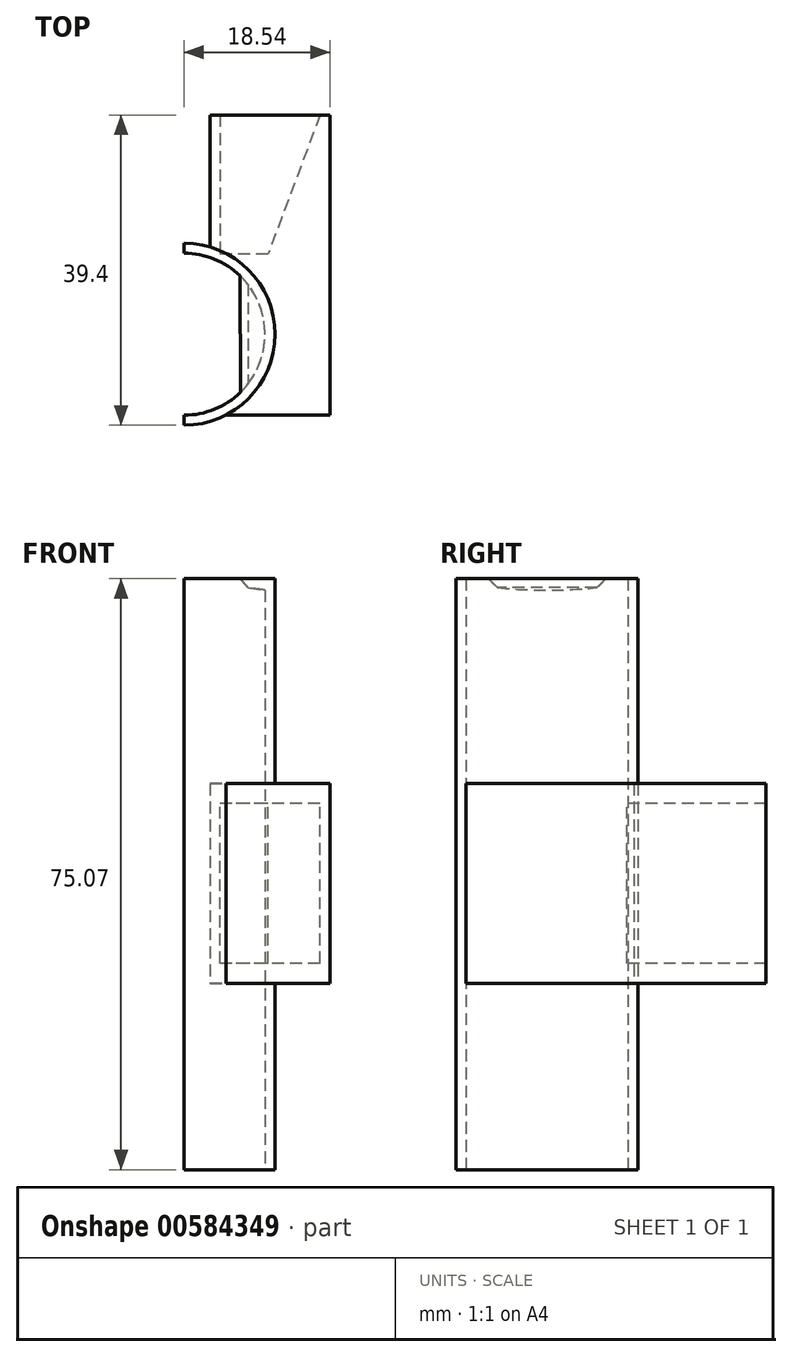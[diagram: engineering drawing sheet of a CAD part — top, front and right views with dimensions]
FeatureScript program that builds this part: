
annotation { "Feature Type Name" : "Feature", "Feature Type Description" : "" }
export const myFeature = defineFeature(function(context is Context, id is Id, definition is map)
    precondition{}
    {
        {
            var Q0;
            Q0=qCreatedBy(makeId("Top.planeOp"),FACE);
            var sketch = newSketch(context, id + "F0", { "sketchPlane" : qUnion([Q0])});
            skArc(sketch, "E0", {"start": v(0, -10.29) * mm, "mid": v(10.29, 0) * mm, "end": v(0, 10.29) * mm});
            skArc(sketch, "E1", {"start": v(0, -11.56) * mm, "mid": v(11.56, 0) * mm, "end": v(0, 11.56) * mm});
            skLineSegment(sketch, "E2", {"start": v(0, 11.56) * mm, "end": v(0, 10.29) * mm});
            skLineSegment(sketch, "E3.trimOffspring", {"start": v(0, -10.29) * mm, "end": v(0, -11.56) * mm});
            skSolve(sketch);
        }
        {
            var Q0;
            Q0=qSketchRegion(id+"F0",true);
            extrude(context, id + "F1", {"entities" : qUnion([Q0]), "endBound" : BoundingType.SYMMETRIC, "depth" : 75.9 * mm});
        }
        {
            var Q0;
            Q0=makeQuery(id+"F1.opExtrude","CAP_FACE",FACE,{"disambiguationData":[OSD([sQuery(id+"F0.wireOp",EDGE,"E0"),sQuery(id+"F0.wireOp",EDGE,"E1"),sQuery(id+"F0.wireOp",EDGE,"E2"),sQuery(id+"F0.wireOp",EDGE,"E3.trimOffspring")])],"isStart":false});
            var sketch = newSketch(context, id + "F2", { "sketchPlane" : qUnion([Q0])});
            skArc(sketch, "E4", {"start": v(0, -11.56) * mm, "mid": v(11.56, 0) * mm, "end": v(0, 11.56) * mm});
            skLineSegment(sketch, "E5", {"start": v(0, 11.56) * mm, "end": v(0, -11.56) * mm});
            skSolve(sketch);
        }
        {
            var Q0;
            Q0=qSketchRegion(id+"F2",true);
            extrude(context, id + "F3", {"entities" : qUnion([Q0]), "operationType" : NewBodyOperationType.ADD, "endBound" : BoundingType.SYMMETRIC, "depth" : 1.52 * mm});
        }
        {
            var Q0;
            Q0=makeQuery(id+"F3.opExtrude","CAP_EDGE",EDGE,{"disambiguationData":[OSD([sQuery(id+"F2.wireOp",EDGE,"E5")])],"isStart":true});
            chamfer(context, id + "F4", {"entities" : qUnion([Q0]), "chamferType" : ChamferType.OFFSET_ANGLE, "width" : 1.52 * mm, "oppositeDirection" : false, "angle" : 82 * degree, "tangentPropagation" : true});
        }
        {
            var Q0;
            Q0=makeQuery(id+"F4.opChamfer","SPLIT",FACE,{"disambiguationData":[OD(0.0)],"derivedFrom":makeQuery(id+"F3.boolean.opBoolean","MERGE",FACE,{"derivedFrom":[makeQuery(id+"F1.opExtrude","SWEPT_FACE",FACE,{"disambiguationData":[OSD([sQuery(id+"F0.wireOp",EDGE,"E2")])]}),makeQuery(id+"F1.opExtrude","SWEPT_FACE",FACE,{"disambiguationData":[OSD([sQuery(id+"F0.wireOp",EDGE,"E3.trimOffspring")])]}),makeQuery(id+"F3.opExtrude","SWEPT_FACE",FACE,{"disambiguationData":[OSD([sQuery(id+"F2.wireOp",EDGE,"E5")])]})]})});
            var sketch = newSketch(context, id + "F5", { "sketchPlane" : qUnion([Q0])});
            skLineSegment(sketch, "E6.bottom", {"start": v(-11.56, -37.95) * mm, "end": v(11.56, -37.95) * mm});
            skLineSegment(sketch, "E6.top", {"start": v(-11.56, -36.36) * mm, "end": v(11.56, -36.36) * mm});
            skLineSegment(sketch, "E6.left", {"start": v(-11.56, -37.95) * mm, "end": v(-11.56, -36.36) * mm});
            skLineSegment(sketch, "E6.right", {"start": v(11.56, -37.95) * mm, "end": v(11.56, -36.36) * mm});
            skSolve(sketch);
        }
        {
            var Q0;
            Q0=qSketchRegion(id+"F5",true);
            extrude(context, id + "F6", {"entities" : qUnion([Q0]), "operationType" : NewBodyOperationType.REMOVE, "oppositeDirection" : true, "depth" : 25.4 * mm});
        }
        {
            var Q0;
            Q0=makeQuery(id+"F6.boolean.opBoolean","COPY",FACE,{"derivedFrom":makeQuery(id+"F6.opExtrude","SWEPT_FACE",FACE,{"disambiguationData":[OSD([sQuery(id+"F5.wireOp",EDGE,"E6.top")])]})});
            cPlane(context, id + "F7", {"entities" : qUnion([Q0]), "cplaneType" : CPlaneType.OFFSET, "offset" : ((3.5 - 0.51) / 2) * mm, "oppositeDirection" : true, "width" : 152.4 * mm, "height" : 152.4 * mm});
        }
        {
            var Q0;
            Q0=makeQuery(id+"F3.opExtrude","CAP_FACE",FACE,{"disambiguationData":[OSD([sQuery(id+"F2.wireOp",EDGE,"E4"),sQuery(id+"F2.wireOp",EDGE,"E5")])],"isStart":false});
            var sketch = newSketch(context, id + "F8", { "sketchPlane" : qUnion([Q0])});
            skLineSegment(sketch, "E7", {"start": v(7, 7.54) * mm, "end": v(7.07, -7.47) * mm});
            skLineSegment(sketch, "E8", {"start": v(0, 11.56) * mm, "end": v(0, -11.56) * mm});
            skPoint(sketch, "E9.center.orphan", {"position": v(0, 0) * mm});
            skArc(sketch, "E10", {"start": v(0, -10.29) * mm, "mid": v(3.8, -9.56) * mm, "end": v(7.07, -7.47) * mm});
            skArc(sketch, "E11.trimOffspring", {"start": v(7, 7.54) * mm, "mid": v(3.76, 9.58) * mm, "end": v(0, 10.29) * mm});
            skSolve(sketch);
        }
        {
            var Q0;
            {var subQ0=sQuery(id+"F8.wireOp",EDGE,"E7");Q0=makeQuery(id+"F8.imprint","IMPRINT",FACE,{"disambiguationData":[TD([[makeQuery(id+"F8.imprint","IMPRINT",EDGE,{"derivedFrom":subQ0}),-1.0]])]});}
            extrude(context, id + "F9", {"entities" : qUnion([Q0]), "operationType" : NewBodyOperationType.REMOVE, "oppositeDirection" : true, "depth" : 25.4 * mm, "offsetDistance" : 25.4 * mm});
        }
        {
            var Q0;
            Q0=makeQuery(id+"F9.boolean.opBoolean","INTERSECT",EDGE,{"derivedFrom":[makeQuery(id+"F4.opChamfer","BLEND_FACE",FACE,{"disambiguationData":[OSD([sQuery(id+"F2.wireOp",EDGE,"E5")])]}),makeQuery(id+"F9.opExtrude","SWEPT_FACE",FACE,{"disambiguationData":[OSD([sQuery(id+"F8.wireOp",EDGE,"E7")])]})]});
            chamfer(context, id + "F10", {"entities" : qUnion([Q0]), "width" : 1.27 * mm, "tangentPropagation" : true});
        }
        {
            var Q0;
            Q0=qCreatedBy(makeId("Front.planeOp"),FACE);
            cPlane(context, id + "F11", {"entities" : qUnion([Q0]), "cplaneType" : CPlaneType.OFFSET, "offset" : 10.16 * mm, "oppositeDirection" : true, "width" : 152.4 * mm, "height" : 152.4 * mm});
        }
        {
            var Q0;
            Q0=qCreatedBy(id+"F11.planeOp",FACE);
            var sketch = newSketch(context, id + "F12", { "sketchPlane" : qUnion([Q0])});
            skLineSegment(sketch, "E12", {"start": v(0, 0) * mm, "end": v(7.62, 0) * mm, "construction": true});
            skLineSegment(sketch, "E13.bottom", {"start": v(10.67, -10.16) * mm, "end": v(4.57, -10.16) * mm});
            skLineSegment(sketch, "E13.top", {"start": v(10.67, 10.16) * mm, "end": v(4.57, 10.16) * mm});
            skLineSegment(sketch, "E13.left", {"start": v(10.67, -10.16) * mm, "end": v(10.67, 10.16) * mm});
            skLineSegment(sketch, "E13.right", {"start": v(4.57, -10.16) * mm, "end": v(4.57, 10.16) * mm});
            skPoint(sketch, "E13.middle", {"position": v(7.62, 0) * mm});
            skSolve(sketch);
        }
        {
            var Q0;
            Q0=qCreatedBy(id+"F11.planeOp",FACE);
            cPlane(context, id + "F13", {"entities" : qUnion([Q0]), "cplaneType" : CPlaneType.OFFSET, "offset" : 17.68 * mm, "oppositeDirection" : true, "width" : 152.4 * mm, "height" : 152.4 * mm});
        }
        {
            var Q0;
            Q0=qCreatedBy(id+"F13.planeOp",FACE);
            var sketch = newSketch(context, id + "F14", { "sketchPlane" : qUnion([Q0])});
            skLineSegment(sketch, "E14.bottom", {"start": v(17.27, -10.16) * mm, "end": v(4.57, -10.16) * mm});
            skLineSegment(sketch, "E14.top", {"start": v(17.27, 10.16) * mm, "end": v(4.57, 10.16) * mm});
            skLineSegment(sketch, "E14.left", {"start": v(17.27, -10.16) * mm, "end": v(17.27, 10.16) * mm});
            skLineSegment(sketch, "E14.right", {"start": v(4.57, -10.16) * mm, "end": v(4.57, 10.16) * mm});
            skPoint(sketch, "E14.middle", {"position": v(10.92, 0) * mm});
            skLineSegment(sketch, "E15.bottom", {"start": v(18.54, -12.7) * mm, "end": v(3.3, -12.7) * mm});
            skLineSegment(sketch, "E15.top", {"start": v(18.54, 12.7) * mm, "end": v(3.3, 12.7) * mm});
            skLineSegment(sketch, "E15.left", {"start": v(18.54, -12.7) * mm, "end": v(18.54, 12.7) * mm});
            skLineSegment(sketch, "E15.right", {"start": v(3.3, -12.7) * mm, "end": v(3.3, 12.7) * mm});
            skSolve(sketch);
        }
        {
            var Q0;
            {var subQ1=sQuery(id+"F14.wireOp",EDGE,"E14.bottom");Q0=makeQuery(id+"F14.imprint","IMPRINT",FACE,{"disambiguationData":[TD([[makeQuery(id+"F14.imprint","IMPRINT",EDGE,{"derivedFrom":subQ1}),-1.0]])]});}
            var Q1;
            {var subQ1=sQuery(id+"F14.wireOp",EDGE,"E14.bottom");Q1=makeQuery(id+"F14.imprint","IMPRINT",FACE,{"disambiguationData":[TD([[makeQuery(id+"F14.imprint","IMPRINT",EDGE,{"derivedFrom":subQ1}),1.0]])]});}
            extrude(context, id + "F15", {"entities" : qUnion([Q0, Q1]), "operationType" : NewBodyOperationType.ADD, "depth" : 38.1 * mm, "offsetDistance" : 25.4 * mm});
        }
        {
            var Q1;
            {var subQ1=sQuery(id+"F14.wireOp",EDGE,"E14.bottom");Q1=makeQuery(id+"F14.imprint","IMPRINT",FACE,{"disambiguationData":[TD([[makeQuery(id+"F14.imprint","IMPRINT",EDGE,{"derivedFrom":subQ1}),-1.0]])]});}
            var Q2;
            {var subQ0=sQuery(id+"F12.wireOp",EDGE,"E13.bottom");Q2=makeQuery(id+"F12.imprint","IMPRINT",FACE,{"disambiguationData":[TD([[makeQuery(id+"F12.imprint","IMPRINT",EDGE,{"derivedFrom":subQ0}),-1.0]])]});}
            loft(context, id + "F16", {"operationType" : NewBodyOperationType.REMOVE, "sheetProfilesArray" : [{ "sheetProfileEntities" : qUnion([Q1]) }, { "sheetProfileEntities" : qUnion([Q2]) }]});
        }
        {
            var Q0;
            {var subQ1=sQuery(id+"F14.wireOp",EDGE,"E15.bottom");Q0=makeQuery(id+"F15.boolean.opBoolean","SPLIT",FACE,{"disambiguationData":[TD([makeQuery(id+"F1.opExtrude","SWEPT_FACE",FACE,{"disambiguationData":[OSD([sQuery(id+"F0.wireOp",EDGE,"E0")])]})])],"derivedFrom":makeQuery(id+"F15.opExtrude","SWEPT_FACE",FACE,{"disambiguationData":[OSD([subQ1])]})});}
            extrude(context, id + "F17", {"entities" : qUnion([Q0]), "operationType" : NewBodyOperationType.REMOVE, "oppositeDirection" : true, "depth" : 25.4 * mm, "offsetDistance" : 25.4 * mm});
        }
    });
